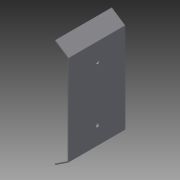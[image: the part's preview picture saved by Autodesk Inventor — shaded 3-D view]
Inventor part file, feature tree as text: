
AUTODESK INVENTOR PART (.ipt)
format: ipt  version: 2015 (Build 190159000, 159)  size: 89,088 bytes
history: native  units: mm
features: extrude x2, sketch x2
ambient origin geometry x8: Origin, YZ Plane, XZ Plane, XY Plane, X Axis, Y Axis, Z Axis, Center Point
bodies: Solid1 (feature_tree)
feature tree (4):
  extrude  "Extrusion1"  Depth=1.0mm
  extrude  "Extrusion2"  Depth=1.0mm
  sketch  "Sketch1"  dims[d0=1.0mm d4=1.0mm]
  sketch  "Sketch2"  dims[d5=52.0mm d6=0.0mm d10=3.0mm d11=3.0mm d12=1.0mm d13=0.0mm]
